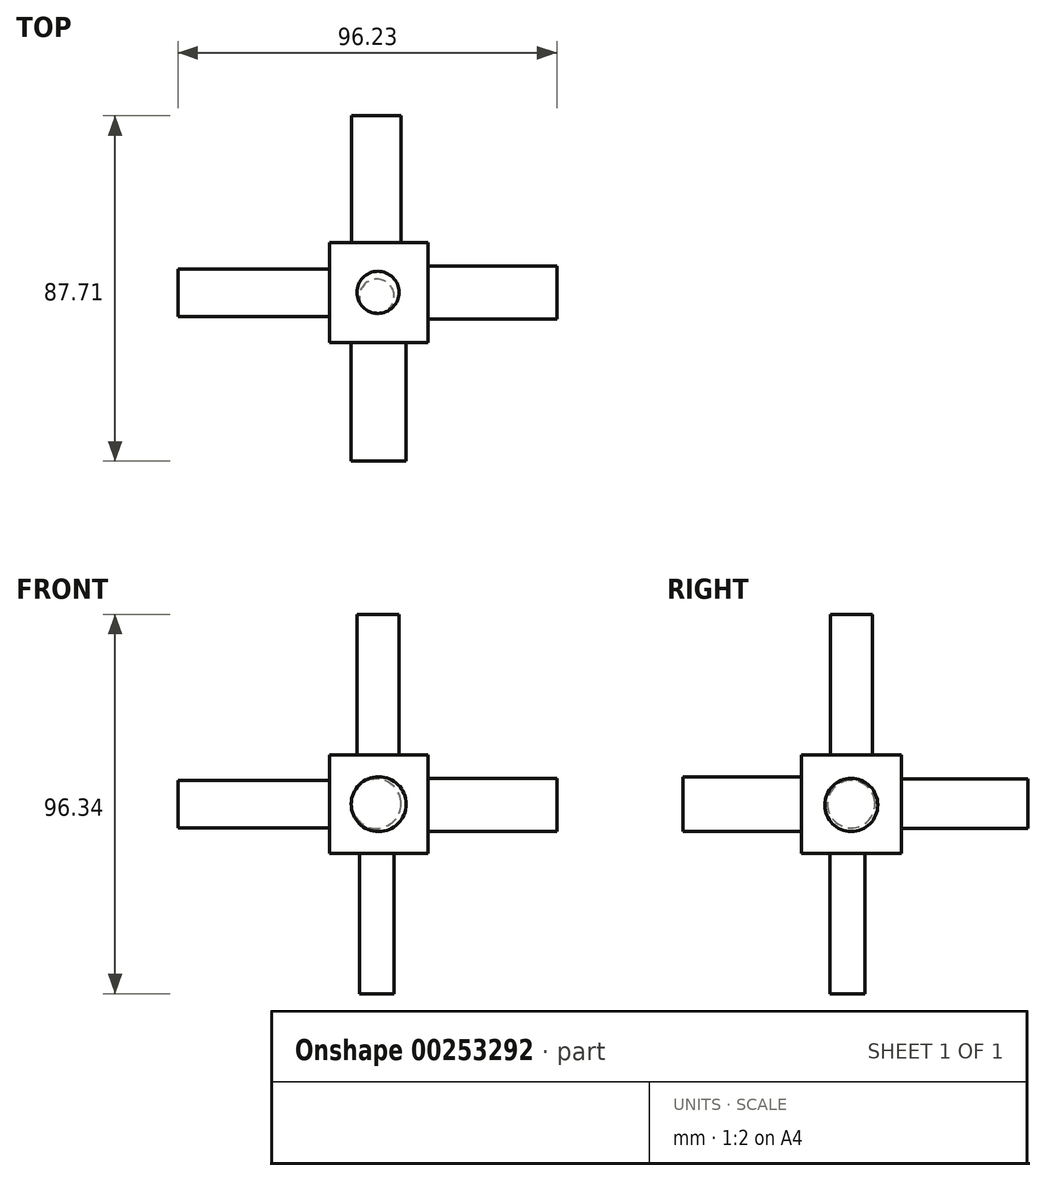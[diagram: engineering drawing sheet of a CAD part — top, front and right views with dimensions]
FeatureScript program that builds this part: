
annotation { "Feature Type Name" : "Feature", "Feature Type Description" : "" }
export const myFeature = defineFeature(function(context is Context, id is Id, definition is map)
    precondition{}
    {
        {
            var Q0;
            Q0=qCreatedBy(makeId("Front.planeOp"),FACE);
            var sketch = newSketch(context, id + "F0", { "sketchPlane" : qUnion([Q0])});
            skLineSegment(sketch, "E0.bottom", {"start": v(0, 0) * mm, "end": v(25, 0) * mm});
            skLineSegment(sketch, "E0.top", {"start": v(0, 25) * mm, "end": v(25, 25) * mm});
            skLineSegment(sketch, "E0.left", {"start": v(0, 0) * mm, "end": v(0, 25) * mm});
            skLineSegment(sketch, "E0.right", {"start": v(25, 0) * mm, "end": v(25, 25) * mm});
            skSolve(sketch);
        }
        {
            var Q0;
            Q0=makeQuery(id+"F0.imprint","IMPRINT",FACE,{"disambiguationData":[TD([[makeQuery(id+"F0.imprint","IMPRINT",EDGE,{"derivedFrom":sQuery(id+"F0.wireOp",EDGE,"E0.bottom")}),1.0]])]});
            extrude(context, id + "F1", {"entities" : qUnion([Q0]), "depth" : 25.4 * mm});
        }
        {
            var Q0;
            Q0=qCreatedBy(makeId("Top.planeOp"),FACE);
            var sketch = newSketch(context, id + "F2", { "sketchPlane" : qUnion([Q0])});
            skCircle(sketch, "E1", {"center": v(12.33, -12.64) * mm, "radius": 5.35 * mm});
            skSolve(sketch);
        }
        {
            var Q0;
            Q0 = qSketchRegion(id + "F2", true);
            extrude(context, id + "F3", {"entities" : qUnion([Q0]), "operationType" : NewBodyOperationType.ADD, "depth" : 60.69 * mm});
        }
        {
            var Q0;
            Q0=qCreatedBy(makeId("Top.planeOp"),FACE);
            var sketch = newSketch(context, id + "F4", { "sketchPlane" : qUnion([Q0])});
            skCircle(sketch, "E2", {"center": v(11.9, -12.26) * mm, "radius": 5.77 * mm});
            skSolve(sketch);
        }
        {
            var Q0;
            Q0=makeQuery(id+"F1.opExtrude","SWEPT_FACE",FACE,{"disambiguationData":[OSD([sQuery(id+"F0.wireOp",EDGE,"E0.bottom")])]});
            var sketch = newSketch(context, id + "F5", { "sketchPlane" : qUnion([Q0])});
            skCircle(sketch, "E3", {"center": v(12.04, 13.71) * mm, "radius": 4.43 * mm});
            skSolve(sketch);
        }
        {
            var Q0;
            Q0 = qSketchRegion(id + "F5", true);
            extrude(context, id + "F6", {"entities" : qUnion([Q0]), "operationType" : NewBodyOperationType.ADD, "depth" : 35.65 * mm});
        }
        {
            var Q0;
            Q0=makeQuery(id+"F4.imprint","IMPRINT",FACE,{"disambiguationData":[TD([[makeQuery(id+"F4.imprint","IMPRINT",EDGE,{"derivedFrom":sQuery(id+"F4.wireOp",EDGE,"E2")}),1.0]])]});
            extrude(context, id + "F7", {"entities" : qUnion([Q0]), "operationType" : NewBodyOperationType.ADD, "depth" : 5.65 * mm});
        }
        {
            var Q0;
            Q0=makeQuery(id+"F0.imprint","IMPRINT",FACE,{"disambiguationData":[TD([[makeQuery(id+"F0.imprint","IMPRINT",EDGE,{"derivedFrom":sQuery(id+"F0.wireOp",EDGE,"E0.bottom")}),1.0]])]});
            var sketch = newSketch(context, id + "F8", { "sketchPlane" : qUnion([Q0])});
            skCircle(sketch, "E4", {"center": v(11.93, 12.61) * mm, "radius": 6.26 * mm});
            skSolve(sketch);
        }
        {
            var Q0;
            Q0 = qSketchRegion(id + "F8", true);
            extrude(context, id + "F9", {"entities" : qUnion([Q0]), "operationType" : NewBodyOperationType.ADD, "oppositeDirection" : true, "depth" : 32.23 * mm});
        }
        {
            var Q0;
            Q0=makeQuery(id+"F1.opExtrude","CAP_FACE",FACE,{"disambiguationData":[OSD([sQuery(id+"F0.wireOp",EDGE,"E0.bottom"),sQuery(id+"F0.wireOp",EDGE,"E0.top"),sQuery(id+"F0.wireOp",EDGE,"E0.left"),sQuery(id+"F0.wireOp",EDGE,"E0.right")])],"isStart":false});
            var sketch = newSketch(context, id + "F10", { "sketchPlane" : qUnion([Q0])});
            skCircle(sketch, "E5", {"center": v(12.5, 12.5) * mm, "radius": 6.98 * mm});
            skPoint(sketch, "E5.centerSnap0", {"position": v(12.5, 0) * mm});
            skPoint(sketch, "E5.centerSnap1", {"position": v(0, 12.5) * mm});
            skSolve(sketch);
        }
        {
            var Q0;
            Q0 = qSketchRegion(id + "F10", true);
            extrude(context, id + "F11", {"entities" : qUnion([Q0]), "operationType" : NewBodyOperationType.ADD, "depth" : 30.08 * mm});
        }
        {
            var Q0;
            Q0=makeQuery(id+"F1.opExtrude","SWEPT_FACE",FACE,{"disambiguationData":[OSD([sQuery(id+"F0.wireOp",EDGE,"E0.right")])]});
            var sketch = newSketch(context, id + "F12", { "sketchPlane" : qUnion([Q0])});
            skCircle(sketch, "E6", {"center": v(-12.7, 12.28) * mm, "radius": 6.74 * mm});
            skPoint(sketch, "E6.centerSnap0", {"position": v(-12.7, 25) * mm});
            skSolve(sketch);
        }
        {
            var Q0;
            Q0 = qSketchRegion(id + "F12", true);
            extrude(context, id + "F13", {"entities" : qUnion([Q0]), "operationType" : NewBodyOperationType.ADD, "depth" : 32.8 * mm});
        }
        {
            var Q0;
            Q0=makeQuery(id+"F1.opExtrude","SWEPT_FACE",FACE,{"disambiguationData":[OSD([sQuery(id+"F0.wireOp",EDGE,"E0.left")])]});
            var sketch = newSketch(context, id + "F14", { "sketchPlane" : qUnion([Q0])});
            skCircle(sketch, "E7", {"center": v(12.73, 12.5) * mm, "radius": 6.04 * mm});
            skPoint(sketch, "E7.centerSnap0", {"position": v(25.4, 12.5) * mm});
            skSolve(sketch);
        }
        {
            var Q0;
            Q0 = qSketchRegion(id + "F14", true);
            extrude(context, id + "F15", {"entities" : qUnion([Q0]), "operationType" : NewBodyOperationType.ADD, "depth" : 38.44 * mm});
        }
    });
